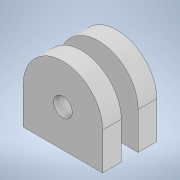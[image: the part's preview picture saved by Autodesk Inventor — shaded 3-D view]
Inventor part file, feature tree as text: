
AUTODESK INVENTOR PART (.ipt)
format: ipt  version: 2021 (Build 250183000, 183)  size: 117,760 bytes
history: native  units: mm
features: plane x2, extrude x1, mirror x1, sketch x1
ambient origin geometry x8: Origin, YZ Plane, XZ Plane, XY Plane, X Axis, Y Axis, Z Axis, Center Point
bodies: Solid1 (feature_tree)
feature tree (5):
  extrude  "Extrusion1"  Depth=10.0mm
  plane  "Work Plane1"
  mirror  "Mirror1"
  plane  "Work Plane2"
  sketch  "Sketch1"  dims[d0=11.0mm d1=18.0mm d2=18.0mm d3=22.0mm d4=90.0deg d5=10.0mm d6=1.0mm d7=0.0mm d8=0.0mm d11=5.0mm d12=0.0mm]
